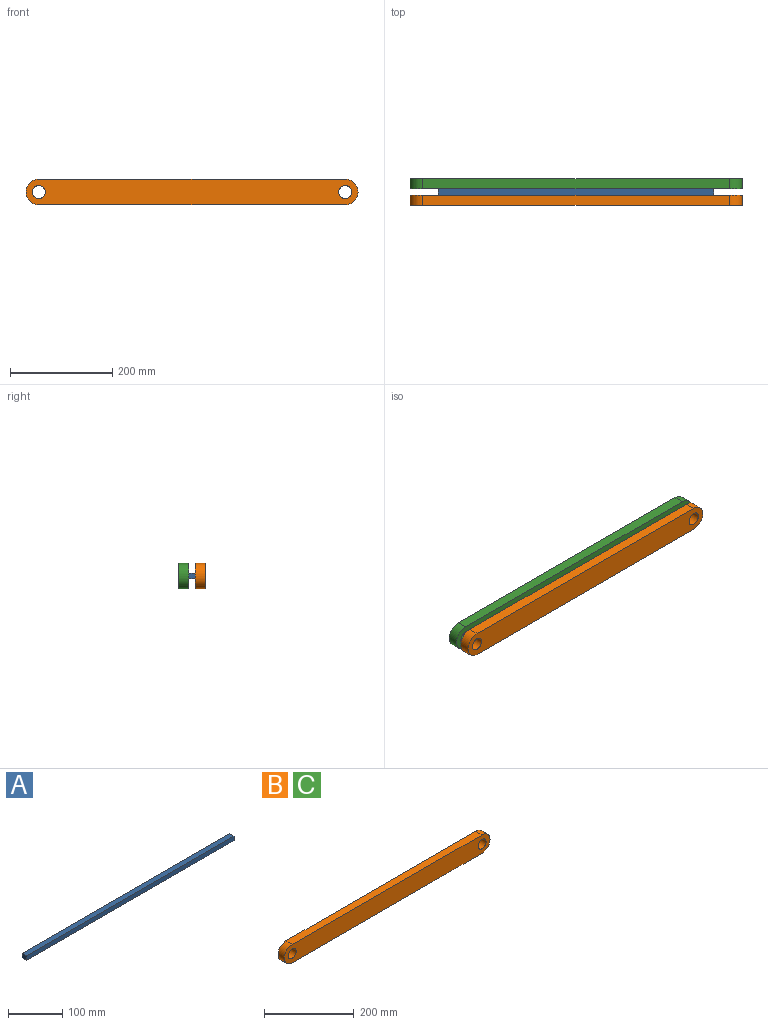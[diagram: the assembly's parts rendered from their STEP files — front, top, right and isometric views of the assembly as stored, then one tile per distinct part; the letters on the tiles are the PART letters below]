
ASSEMBLY  parts=3 mates=2
PART A: 6 faces, bbox 540x12x10 mm
  f0: plane 540x12mm, normal (0,0,-1), area 6480mm2, adj f1,f3,f4,f5
  f1: plane 12x10mm, normal (1,0,0), area 120mm2, adj f0,f2,f4,f5
  f2: plane 540x12mm, normal (0,0,1), area 6480mm2, adj f1,f3,f4,f5
  f3: plane 12x10mm, normal (-1,0,0), area 120mm2, adj f0,f2,f4,f5
  f4: plane 540x10mm, normal (0,1,0), area 5400mm2, adj f0,f1,f2,f3
  f5: plane 540x10mm, normal (0,-1,0), area 5400mm2, adj f0,f1,f2,f3
PART B: 8 faces, bbox 650x20x50 mm
  f0: cylinder r=25mm len=50mm, axis (0,1,0), area 1570.8mm2, adj f1,f4,f6,f7
  f1: plane 600x20mm, normal (0,0,-1), area 12000mm2, adj f0,f2,f6,f7
  f2: cylinder r=25mm len=50mm, axis (0,1,0), area 1570.8mm2, adj f1,f4,f6,f7
  f3: cylinder r=12.75mm len=25.5mm, axis (0,1,0), area 1602.2mm2, adj f6,f7
  f4: plane 600x20mm, normal (0,0,1), area 12000mm2, adj f0,f2,f6,f7
  f5: cylinder r=12.75mm len=25.5mm, axis (0,1,0), area 1602.2mm2, adj f6,f7
  f6: plane 650x50mm, normal (0,-1,0), area 30942.1mm2, adj f0,f1,f2,f3,f4,f5
  f7: plane 650x50mm, normal (0,1,0), area 30942.1mm2, adj f0,f1,f2,f3,f4,f5
PART C: same geometry as B
PLACE A t=(-188.91,-176.25,103.33)mm
PLACE B t=(-188.91,-176.25,103.33)mm
PLACE C t=(-188.91,-144.25,103.33)mm
MATE fastened B.f0 <-> C.f0  axis (0,1,0) through (-488.91,-176.25,48.33)mm
MATE fastened C.f6 <-> A.f4  axis (0,-1,0) through (-188.91,-164.25,48.33)mm
